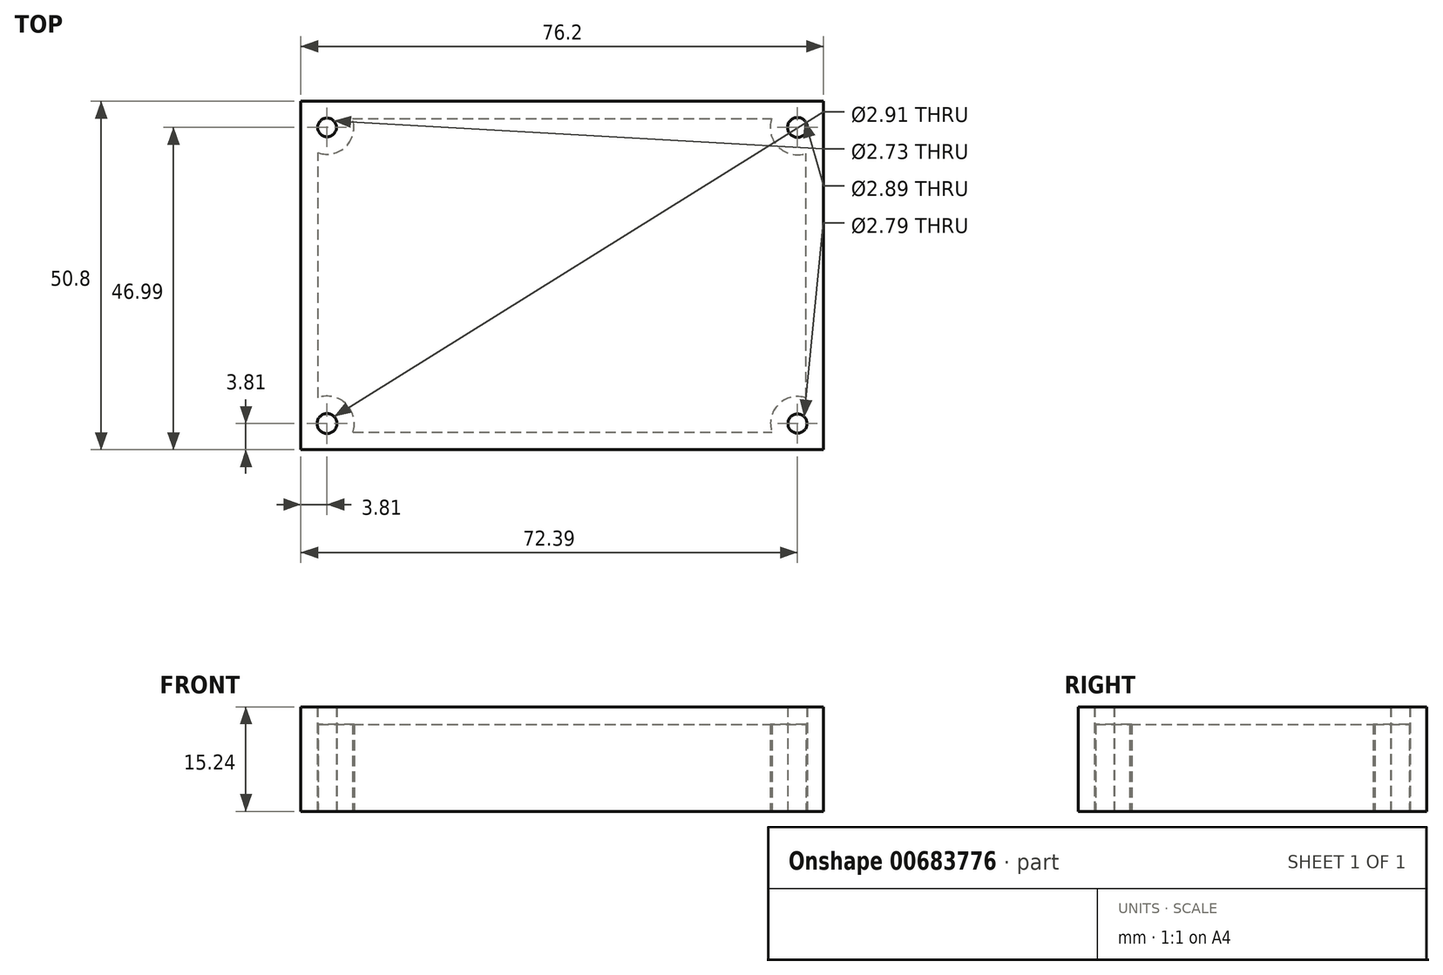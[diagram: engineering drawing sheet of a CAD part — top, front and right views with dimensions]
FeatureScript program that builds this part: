
annotation { "Feature Type Name" : "Feature", "Feature Type Description" : "" }
export const myFeature = defineFeature(function(context is Context, id is Id, definition is map)
    precondition{}
    {
        {
            var Q0;
            Q0=qCreatedBy(makeId("Top.planeOp"),FACE);
            var sketch = newSketch(context, id + "F0", { "sketchPlane" : qUnion([Q0])});
            skLineSegment(sketch, "E0.bottom", {"start": v(0, 0) * mm, "end": v(76.2, 0) * mm});
            skLineSegment(sketch, "E0.top", {"start": v(0, 50.8) * mm, "end": v(76.2, 50.8) * mm});
            skLineSegment(sketch, "E0.left", {"start": v(0, 0) * mm, "end": v(0, 50.8) * mm});
            skLineSegment(sketch, "E0.right", {"start": v(76.2, 0) * mm, "end": v(76.2, 50.8) * mm});
            skLineSegment(sketch, "E1.top", {"start": v(0, 44.45) * mm, "end": v(76.2, 44.45) * mm});
            skLineSegment(sketch, "E1.left", {"start": v(0, 50.8) * mm, "end": v(0, 44.45) * mm});
            skLineSegment(sketch, "E1.right", {"start": v(76.2, 50.8) * mm, "end": v(76.2, 44.45) * mm});
            skLineSegment(sketch, "E2.bottom", {"start": v(0, 6.35) * mm, "end": v(76.2, 6.35) * mm});
            skLineSegment(sketch, "E2.left", {"start": v(0, 6.35) * mm, "end": v(0, 0) * mm});
            skLineSegment(sketch, "E2.right", {"start": v(76.2, 6.35) * mm, "end": v(76.2, 0) * mm});
            skLineSegment(sketch, "E3.bottom", {"start": v(0, 44.45) * mm, "end": v(16.5, 44.45) * mm});
            skLineSegment(sketch, "E3.top", {"start": v(0, 6.35) * mm, "end": v(16.5, 6.35) * mm});
            skLineSegment(sketch, "E3.left", {"start": v(0, 44.45) * mm, "end": v(0, 6.35) * mm});
            skLineSegment(sketch, "E3.right", {"start": v(16.5, 44.45) * mm, "end": v(16.5, 6.35) * mm});
            skLineSegment(sketch, "E4.bottom", {"start": v(63.5, 44.45) * mm, "end": v(76.2, 44.45) * mm});
            skLineSegment(sketch, "E4.top", {"start": v(63.5, 6.35) * mm, "end": v(76.2, 6.35) * mm});
            skLineSegment(sketch, "E4.left", {"start": v(63.5, 44.45) * mm, "end": v(63.5, 6.35) * mm});
            skLineSegment(sketch, "E4.right", {"start": v(76.2, 44.45) * mm, "end": v(76.2, 6.35) * mm});
            skLineSegment(sketch, "E5.bottom", {"start": v(0, 50.8) * mm, "end": v(3.8, 50.8) * mm});
            skLineSegment(sketch, "E5.left", {"start": v(0, 50.8) * mm, "end": v(0, 47) * mm});
            skCircle(sketch, "E6", {"center": v(3.8, 47) * mm, "radius": 1.37 * mm});
            skLineSegment(sketch, "E7.bottom", {"start": v(76.2, 50.8) * mm, "end": v(72.4, 50.8) * mm});
            skLineSegment(sketch, "E7.left", {"start": v(76.2, 50.8) * mm, "end": v(76.2, 47) * mm});
            skLineSegment(sketch, "E8.bottom", {"start": v(76.2, 0) * mm, "end": v(72.4, 0) * mm});
            skLineSegment(sketch, "E8.left", {"start": v(76.2, 0) * mm, "end": v(76.2, 3.81) * mm});
            skPoint(sketch, "E9.oppositeSnap0", {"position": v(0, 3.18) * mm});
            skLineSegment(sketch, "E9.left", {"start": v(0, 0) * mm, "end": v(0, 3.18) * mm});
            skLineSegment(sketch, "E10.bottom", {"start": v(0, 0) * mm, "end": v(3.81, 0) * mm});
            skLineSegment(sketch, "E10.left", {"start": v(0, 0) * mm, "end": v(0, 3.8) * mm});
            skCircle(sketch, "E11", {"center": v(3.8, 3.8) * mm, "radius": 1.45 * mm});
            skCircle(sketch, "E12", {"center": v(72.4, 3.8) * mm, "radius": 1.4 * mm});
            skCircle(sketch, "E13", {"center": v(72.4, 47) * mm, "radius": 1.45 * mm});
            skSolve(sketch);
        }
        {
            var Q0;
            Q0=makeQuery(id+"F0.imprint","IMPRINT",FACE,{"disambiguationData":[TD([[makeQuery(id+"F0.imprint","IMPRINT",EDGE,{"derivedFrom":sQuery(id+"F0.wireOp",EDGE,"E0.top")}),-1.0]])]});
            var Q1;
            Q1=makeQuery(id+"F0.imprint","IMPRINT",FACE,{"disambiguationData":[TD([[makeQuery(id+"F0.imprint","IMPRINT",EDGE,{"derivedFrom":sQuery(id+"F0.wireOp",EDGE,"E1.top")}),-1.0]])]});
            var Q2;
            Q2=makeQuery(id+"F0.imprint","IMPRINT",FACE,{"disambiguationData":[TD([[makeQuery(id+"F0.imprint","IMPRINT",EDGE,{"derivedFrom":sQuery(id+"F0.wireOp",EDGE,"E2.bottom")}),-1.0]])]});
            extrude(context, id + "F1", {"entities" : qUnion([Q0, Q1, Q2]), "depth" : 15.24 * mm, "offsetDistance" : 25.4 * mm});
        }
        {
            var Q0;
            Q0=makeQuery(id+"F1.opExtrude","CAP_FACE",FACE,{"disambiguationData":[OSD([sQuery(id+"F0.wireOp",EDGE,"E0.top"),sQuery(id+"F0.wireOp",EDGE,"E1.left"),sQuery(id+"F0.wireOp",EDGE,"E1.right"),sQuery(id+"F0.wireOp",EDGE,"E0.bottom"),sQuery(id+"F0.wireOp",EDGE,"E2.left"),sQuery(id+"F0.wireOp",EDGE,"E2.right"),sQuery(id+"F0.wireOp",EDGE,"E3.bottom"),sQuery(id+"F0.wireOp",EDGE,"E3.top"),sQuery(id+"F0.wireOp",EDGE,"E3.right"),sQuery(id+"F0.wireOp",EDGE,"E4.bottom"),sQuery(id+"F0.wireOp",EDGE,"E4.top"),sQuery(id+"F0.wireOp",EDGE,"E4.left")])],"isStart":true});
            shell(context, id + "F2", {"entities" : qUnion([Q0]), "thickness" : 2.54 * mm});
        }
    });
